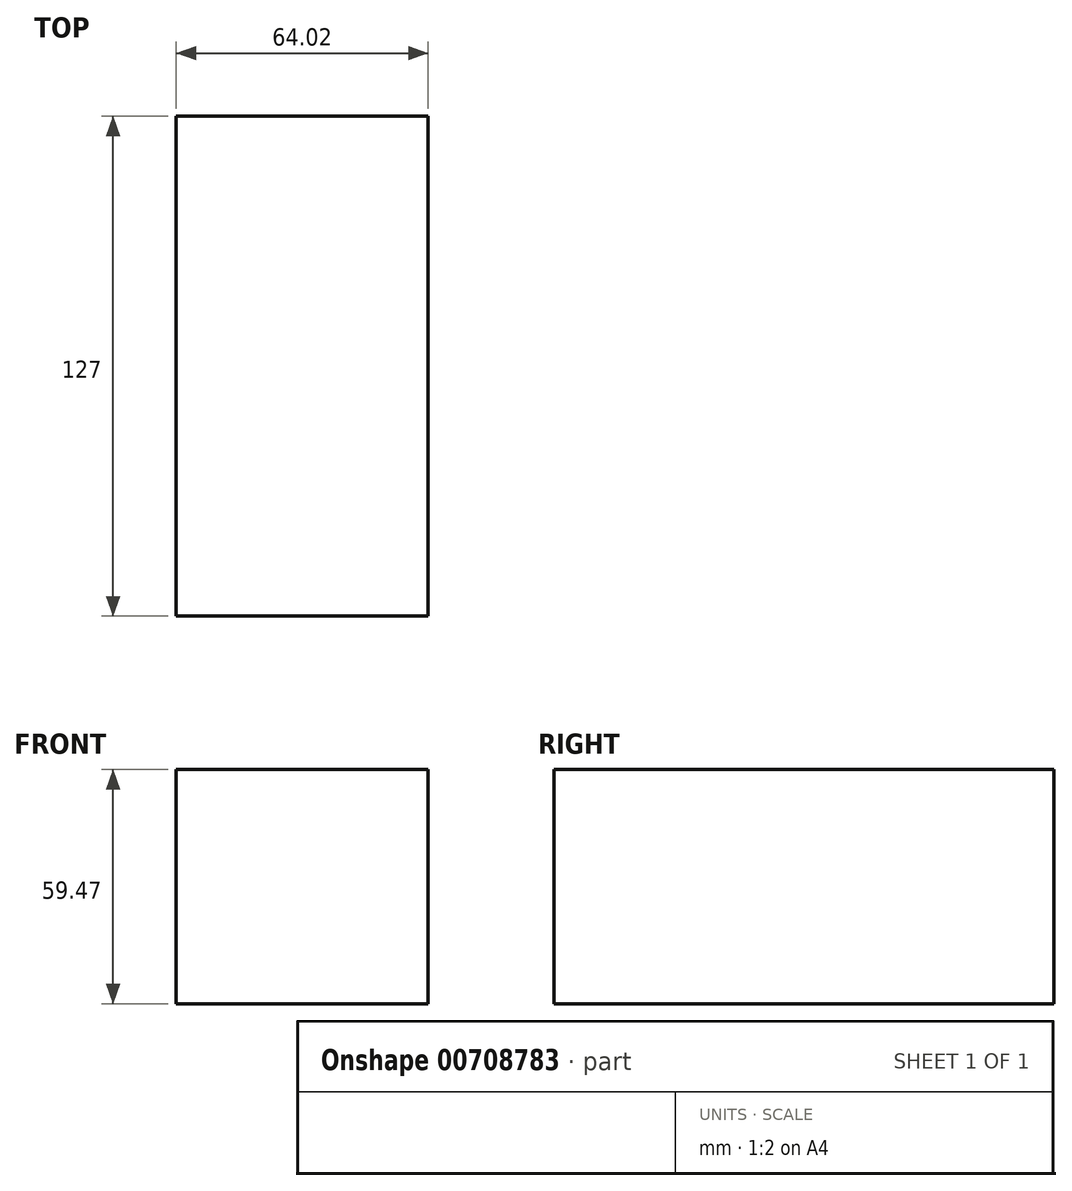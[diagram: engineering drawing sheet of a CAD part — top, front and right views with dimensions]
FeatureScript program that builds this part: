
annotation { "Feature Type Name" : "Feature", "Feature Type Description" : "" }
export const myFeature = defineFeature(function(context is Context, id is Id, definition is map)
    precondition{}
    {
        {
            var Q0;
            Q0=qCreatedBy(makeId("Front.planeOp"),FACE);
            var sketch = newSketch(context, id + "F0", { "sketchPlane" : qUnion([Q0])});
            skLineSegment(sketch, "E0.bottom", {"start": v(0, 0) * mm, "end": v(64.02, 0) * mm});
            skLineSegment(sketch, "E0.top", {"start": v(0, 59.47) * mm, "end": v(64.02, 59.47) * mm});
            skLineSegment(sketch, "E0.left", {"start": v(0, 0) * mm, "end": v(0, 59.47) * mm});
            skLineSegment(sketch, "E0.right", {"start": v(64.02, 0) * mm, "end": v(64.02, 59.47) * mm});
            skSolve(sketch);
        }
        {
            var Q0;
            Q0=makeQuery(id+"F0.imprint","IMPRINT",FACE,{"disambiguationData":[TD([[makeQuery(id+"F0.imprint","IMPRINT",EDGE,{"derivedFrom":sQuery(id+"F0.wireOp",EDGE,"E0.bottom")}),1.0]])]});
            extrude(context, id + "F1", {"entities" : qUnion([Q0]), "depth" : 127 * mm, "offsetDistance" : 25.4 * mm});
        }
    });
